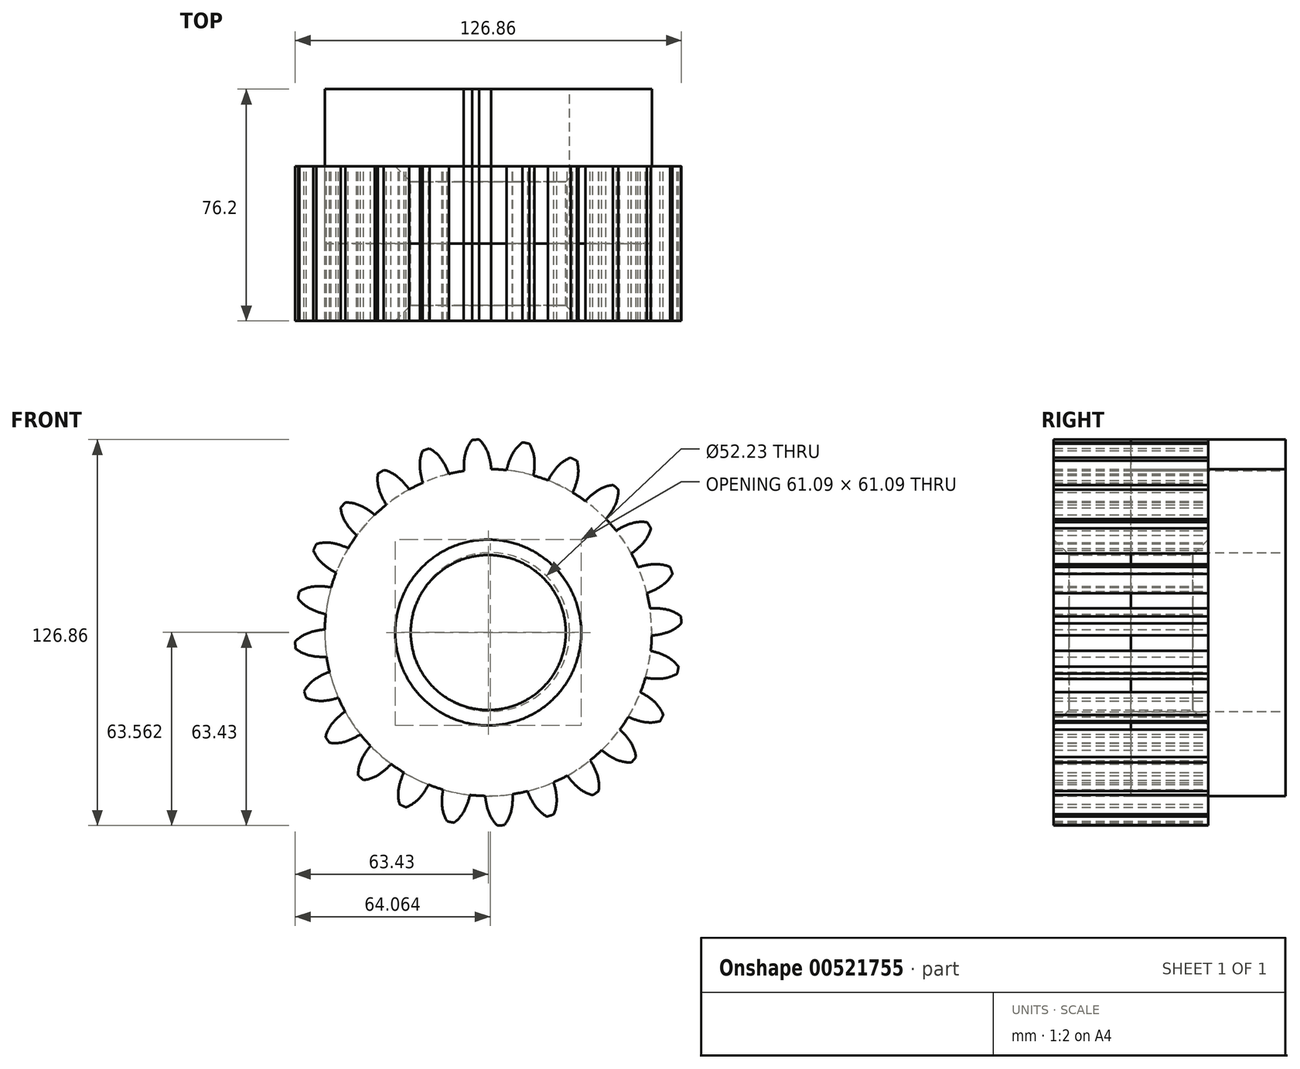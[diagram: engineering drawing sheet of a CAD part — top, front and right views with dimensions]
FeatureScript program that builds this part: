
annotation { "Feature Type Name" : "Feature", "Feature Type Description" : "" }
export const myFeature = defineFeature(function(context is Context, id is Id, definition is map)
    precondition{}
    {
        {
            var Q0;
            Q0=qCreatedBy(makeId("Front.planeOp"),FACE);
            var sketch = newSketch(context, id + "F0", { "sketchPlane" : qUnion([Q0])});
            skCircle(sketch, "E0", {"center": v(0, 0) * mm, "radius": 53.72 * mm});
            skCircle(sketch, "E1", {"center": v(0, 0) * mm, "radius": 58.67 * mm, "construction": true});
            skCircle(sketch, "E2", {"center": v(0, 0) * mm, "radius": 4.3 * mm, "construction": true});
            skCircle(sketch, "E3", {"center": v(0, 0) * mm, "radius": 63.5 * mm, "construction": true});
            skLineSegment(sketch, "E4", {"start": v(0, 0) * mm, "end": v(0, 123.07) * mm, "construction": true});
            skLineSegment(sketch, "E5", {"start": v(0, 0) * mm, "end": v(-6.38, 97.3) * mm, "construction": true});
            skLineSegment(sketch, "E6", {"start": v(0, 58.67) * mm, "end": v(-73.35, 58.67) * mm, "construction": true});
            skLineSegment(sketch, "E7", {"start": v(0, 58.67) * mm, "end": v(-73.35, 31.98) * mm, "construction": true});
            skCircle(sketch, "E8", {"center": v(0, 0) * mm, "radius": 55.14 * mm, "construction": true});
            skCircle(sketch, "E9", {"center": v(0, 58.67) * mm, "radius": 14.6 * mm, "construction": true});
            skCircle(sketch, "E10", {"center": v(-13.63, 53.42) * mm, "radius": 14.6 * mm, "construction": true});
            skArc(sketch, "E11", {"start": v(0.97, 53.71) * mm, "mid": v(0.64, 56.22) * mm, "end": v(0, 58.67) * mm});
            skArc(sketch, "E12", {"start": v(0, 58.67) * mm, "mid": v(-1.2, 61.23) * mm, "end": v(-2.99, 63.43) * mm});
            skArc(sketch, "E13.MirrorCS", {"start": v(-7.66, 58.17) * mm, "mid": v(-6.8, 60.87) * mm, "end": v(-5.32, 63.28) * mm});
            skArc(sketch, "E14.MirrorCS", {"start": v(-7.98, 53.13) * mm, "mid": v(-7.98, 55.66) * mm, "end": v(-7.66, 58.17) * mm});
            skArc(sketch, "E15", {"start": v(-2.99, 63.43) * mm, "mid": v(-4.15, 63.39) * mm, "end": v(-5.32, 63.28) * mm});
            skCircle(sketch, "E16", {"center": v(0.63, 0.13) * mm, "radius": 26.11 * mm});
            skSolve(sketch);
        }
        {
            var Q0;
            {var subQ0=sQuery(id+"F0.wireOp",EDGE,"E11");Q0=makeQuery(id+"F0.imprint","IMPRINT",FACE,{"disambiguationData":[TD([[makeQuery(id+"F0.imprint","IMPRINT",EDGE,{"derivedFrom":subQ0}),1.0]])]});}
            var Q1;
            {var subQ0=sQuery(id+"F0.wireOp",EDGE,"E0");var subQ1=makeQuery(id+"F0.imprint","INTERSECT",VERTEX,{"derivedFrom":[subQ0,sQuery(id+"F0.wireOp",EDGE,"E11")]});Q1=makeQuery(id+"F0.imprint","IMPRINT",FACE,{"disambiguationData":[TD([[makeQuery(id+"F0.imprint","IMPRINT",EDGE,{"disambiguationData":[TD([[subQ1,-1.0]])],"derivedFrom":subQ0}),1.0]])]});}
            extrude(context, id + "F1", {"entities" : qUnion([Q0, Q1]), "depth" : 50.8 * mm, "offsetDistance" : 25.4 * mm});
        }
        {
            var Q0;
            Q0=makeQuery(id+"F1.opExtrude","SWEPT_BODY",BODY,{"disambiguationData":[OSD([sQuery(id+"F0.wireOp",EDGE,"E0"),sQuery(id+"F0.wireOp",EDGE,"E11"),sQuery(id+"F0.wireOp",EDGE,"E12"),sQuery(id+"F0.wireOp",EDGE,"E13.MirrorCS"),sQuery(id+"F0.wireOp",EDGE,"E14.MirrorCS"),sQuery(id+"F0.wireOp",EDGE,"E15")])]});
            var Q1;
            Q1=makeQuery(id+"F1.opExtrude","SWEPT_FACE",FACE,{"disambiguationData":[OSD([sQuery(id+"F0.wireOp",EDGE,"E0")])]});
            circularPattern(context, id + "F2", {"operationType" : NewBodyOperationType.ADD, "entities" : qUnion([Q0]), "axis" : qUnion([Q1]), "angle" : 360 * degree, "instanceCount" : 24, "equalSpace" : true});
        }
        {
            var Q0;
            Q0=makeQuery(id+"F2.opPattern","COPY",EDGE,{"derivedFrom":makeQuery(id+"F1.opExtrude","CAP_EDGE",EDGE,{"disambiguationData":[OSD([sQuery(id+"F0.wireOp",EDGE,"E16")])],"isStart":false}),"instanceName":"16"});
            var Q1;
            Q1=makeQuery(id+"F2.opPattern","COPY",EDGE,{"derivedFrom":makeQuery(id+"F1.opExtrude","CAP_EDGE",EDGE,{"disambiguationData":[OSD([sQuery(id+"F0.wireOp",EDGE,"E16")])],"isStart":true}),"instanceName":"23"});
            chamfer(context, id + "F3", {"entities" : qUnion([Q0, Q1]), "width" : 5.08 * mm, "tangentPropagation" : true});
        }
        {
            var Q0;
            Q0=makeQuery(id+"F0.imprint","IMPRINT",FACE,{"disambiguationData":[TD([[makeQuery(id+"F0.imprint","IMPRINT",EDGE,{"derivedFrom":sQuery(id+"F0.wireOp",EDGE,"E16")}),-1.0]])]});
            var Q1;
            {var subQ0=sQuery(id+"F0.wireOp",EDGE,"E11");Q1=makeQuery(id+"F0.imprint","IMPRINT",FACE,{"disambiguationData":[TD([[makeQuery(id+"F0.imprint","IMPRINT",EDGE,{"derivedFrom":subQ0}),1.0]])]});}
            extrude(context, id + "F4", {"entities" : qUnion([Q0, Q1]), "endBound" : BoundingType.SYMMETRIC, "depth" : 50.8 * mm, "offsetDistance" : 25.4 * mm});
        }
    });
